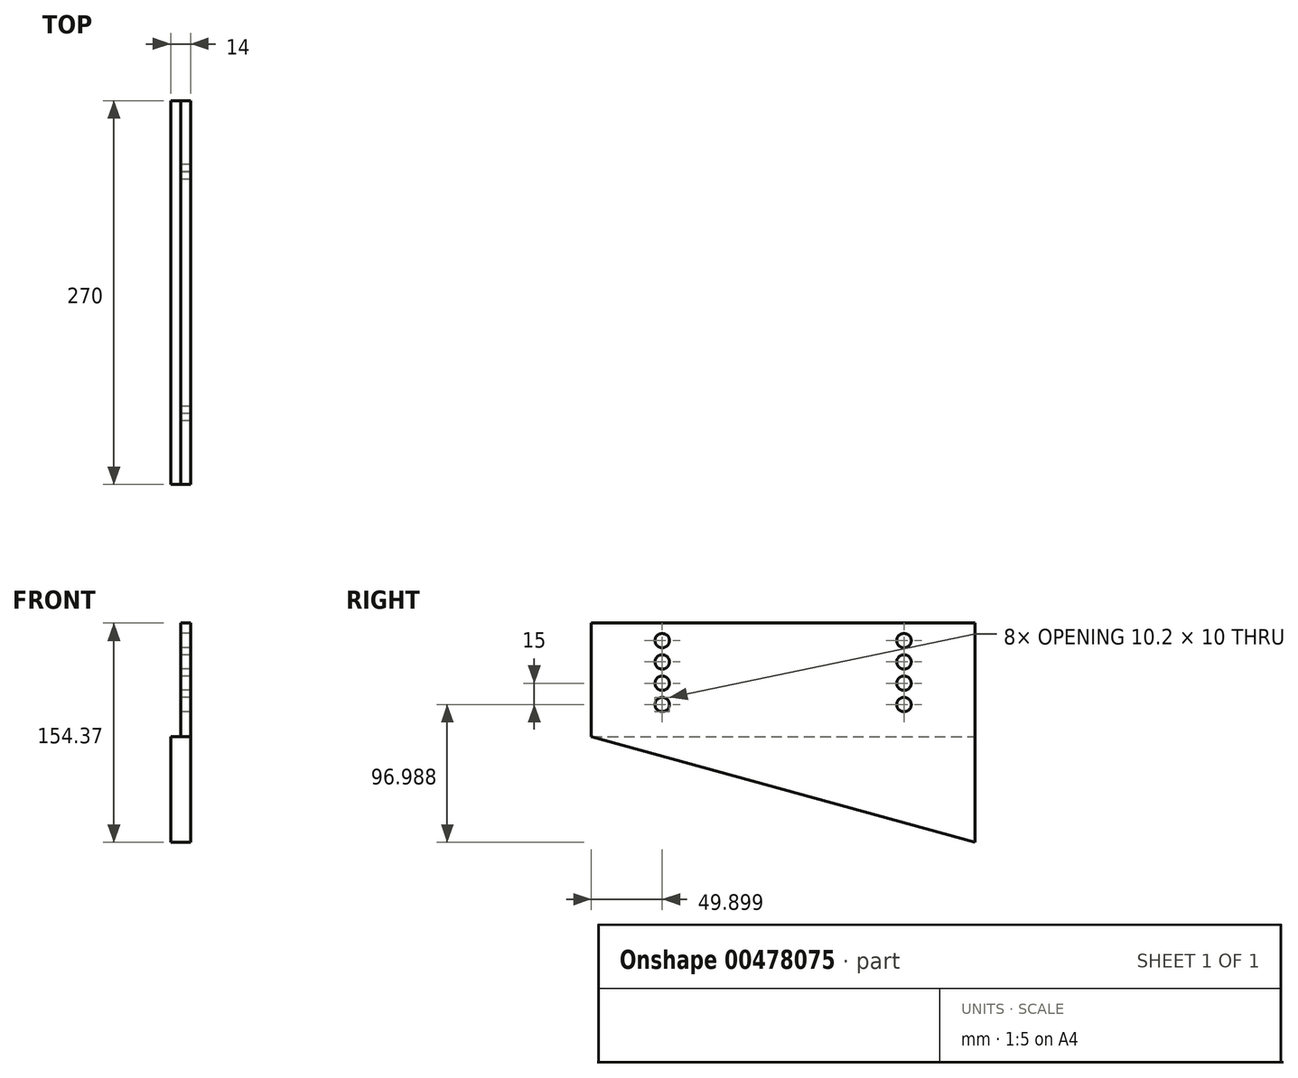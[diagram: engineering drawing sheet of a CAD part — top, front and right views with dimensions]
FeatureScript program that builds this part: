
annotation { "Feature Type Name" : "Feature", "Feature Type Description" : "" }
export const myFeature = defineFeature(function(context is Context, id is Id, definition is map)
    precondition{}
    {
        {
            var Q0;
            Q0=qCreatedBy(makeId("Right.planeOp"),FACE);
            var sketch = newSketch(context, id + "F0", { "sketchPlane" : qUnion([Q0])});
            skLineSegment(sketch, "E0", {"start": v(-152.41, 80) * mm, "end": v(117.59, 80) * mm});
            skLineSegment(sketch, "E1", {"start": v(117.59, -74.37) * mm, "end": v(117.59, 80) * mm});
            skLineSegment(sketch, "E2", {"start": v(-102.41, 80) * mm, "end": v(67.59, 80) * mm});
            skLineSegment(sketch, "E3", {"start": v(117.59, -74.37) * mm, "end": v(-152.41, 0) * mm});
            skLineSegment(sketch, "E4", {"start": v(117.59, 0) * mm, "end": v(-152.41, 0) * mm});
            skLineSegment(sketch, "E5", {"start": v(-152.41, 80) * mm, "end": v(-152.41, 0) * mm});
            skCircle(sketch, "E6", {"center": v(-102.41, 67.62) * mm, "radius": 5 * mm});
            skCircle(sketch, "E7", {"center": v(67.59, 67.62) * mm, "radius": 5 * mm});
            skCircle(sketch, "E8.0.1.0", {"center": v(67.59, 52.62) * mm, "radius": 5 * mm});
            skCircle(sketch, "E8.0.1.1", {"center": v(-102.41, 52.62) * mm, "radius": 5 * mm});
            skCircle(sketch, "E8.0.2.0", {"center": v(67.59, 37.62) * mm, "radius": 5 * mm});
            skCircle(sketch, "E8.0.2.1", {"center": v(-102.41, 37.62) * mm, "radius": 5 * mm});
            skCircle(sketch, "E8.0.3.0", {"center": v(67.59, 22.62) * mm, "radius": 5 * mm});
            skCircle(sketch, "E8.0.3.1", {"center": v(-102.41, 22.62) * mm, "radius": 5 * mm});
            skCircle(sketch, "E8.1.0.0", {"center": v(67.49, 67.62) * mm, "radius": 5 * mm});
            skCircle(sketch, "E8.1.0.1", {"center": v(-102.51, 67.62) * mm, "radius": 5 * mm});
            skCircle(sketch, "E8.1.1.0", {"center": v(67.49, 52.62) * mm, "radius": 5 * mm});
            skCircle(sketch, "E8.1.1.1", {"center": v(-102.51, 52.62) * mm, "radius": 5 * mm});
            skCircle(sketch, "E8.1.2.0", {"center": v(67.49, 37.62) * mm, "radius": 5 * mm});
            skCircle(sketch, "E8.1.2.1", {"center": v(-102.51, 37.62) * mm, "radius": 5 * mm});
            skCircle(sketch, "E8.1.3.0", {"center": v(67.49, 22.62) * mm, "radius": 5 * mm});
            skCircle(sketch, "E8.1.3.1", {"center": v(-102.51, 22.62) * mm, "radius": 5 * mm});
            skCircle(sketch, "E8.2.0.0", {"center": v(67.39, 67.62) * mm, "radius": 5 * mm});
            skCircle(sketch, "E8.2.0.1", {"center": v(-102.61, 67.62) * mm, "radius": 5 * mm});
            skCircle(sketch, "E8.2.1.0", {"center": v(67.39, 52.62) * mm, "radius": 5 * mm});
            skCircle(sketch, "E8.2.1.1", {"center": v(-102.61, 52.62) * mm, "radius": 5 * mm});
            skCircle(sketch, "E8.2.2.0", {"center": v(67.39, 37.62) * mm, "radius": 5 * mm});
            skCircle(sketch, "E8.2.2.1", {"center": v(-102.61, 37.62) * mm, "radius": 5 * mm});
            skCircle(sketch, "E8.2.3.0", {"center": v(67.39, 22.62) * mm, "radius": 5 * mm});
            skCircle(sketch, "E8.2.3.1", {"center": v(-102.61, 22.62) * mm, "radius": 5 * mm});
            skLineSegment(sketch, "E8.direction1", {"start": v(67.59, 67.62) * mm, "end": v(67.49, 67.62) * mm, "construction": true});
            skLineSegment(sketch, "E8.direction2", {"start": v(67.59, 67.62) * mm, "end": v(67.59, 52.62) * mm, "construction": true});
            skSolve(sketch);
        }
        {
            var Q0;
            {var subQ0=sQuery(id+"F0.wireOp",EDGE,"E5");Q0=makeQuery(id+"F0.imprint","IMPRINT",FACE,{"disambiguationData":[TD([[makeQuery(id+"F0.imprint","IMPRINT",EDGE,{"derivedFrom":subQ0}),1.0]])]});}
            var Q1;
            {var subQ5=sQuery(id+"F0.wireOp",EDGE,"kZBZgwTT-XFhY-glHP-XGmq-IiVmHmRIZegb");var subQ6=sQuery(id+"F0.wireOp",EDGE,"E4");var subQ7=makeQuery(id+"F0.imprint","INTERSECT",VERTEX,{"derivedFrom":[subQ6,subQ5]});Q1=makeQuery(id+"F0.imprint","IMPRINT",FACE,{"disambiguationData":[TD([[makeQuery(id+"F0.imprint","IMPRINT",EDGE,{"disambiguationData":[TD([[subQ7,1.0]])],"derivedFrom":subQ6}),-1.0]])]});}
            var Q2;
            {var subQ1=sQuery(id+"F0.wireOp",EDGE,"E2");Q2=makeQuery(id+"F0.imprint","IMPRINT",FACE,{"disambiguationData":[TD([[makeQuery(id+"F0.imprint","IMPRINT",EDGE,{"derivedFrom":subQ1}),-1.0]])]});}
            var Q3;
            {var subQ1=sQuery(id+"F0.wireOp",EDGE,"E0");var subQ5=sQuery(id+"F0.wireOp",EDGE,"E1");var subQ6=makeQuery(id+"F0.imprint","INTERSECT",VERTEX,{"derivedFrom":[subQ1,subQ5]});Q3=makeQuery(id+"F0.imprint","IMPRINT",FACE,{"disambiguationData":[TD([[makeQuery(id+"F0.imprint","IMPRINT",EDGE,{"disambiguationData":[TD([[subQ6,1.0]])],"derivedFrom":subQ5}),1.0]])]});}
            var Q4;
            {var subQ4=sQuery(id+"F0.wireOp",EDGE,"E3");Q4=makeQuery(id+"F0.imprint","IMPRINT",FACE,{"disambiguationData":[TD([[makeQuery(id+"F0.imprint","IMPRINT",EDGE,{"derivedFrom":subQ4}),-1.0]])]});}
            extrude(context, id + "F1", {"entities" : qUnion([Q0, Q1, Q2, Q3, Q4]), "depth" : 7 * mm});
        }
        {
            var Q0;
            Q0=makeQuery(id+"F1.opExtrude","CAP_FACE",FACE,{"disambiguationData":[OSD([sQuery(id+"F0.wireOp",EDGE,"E0"),sQuery(id+"F0.wireOp",EDGE,"E1"),sQuery(id+"F0.wireOp",EDGE,"E2"),sQuery(id+"F0.wireOp",EDGE,"E3"),sQuery(id+"F0.wireOp",EDGE,"E5"),sQuery(id+"F0.wireOp",EDGE,"E6"),sQuery(id+"F0.wireOp",EDGE,"E7")])],"isStart":true});
            var sketch = newSketch(context, id + "F2", { "sketchPlane" : qUnion([Q0])});
            skLineSegment(sketch, "E9", {"start": v(152.41, 0) * mm, "end": v(-117.59, 0) * mm});
            skLineSegment(sketch, "E10", {"start": v(-117.59, 0) * mm, "end": v(-117.59, -74.37) * mm});
            skLineSegment(sketch, "E11", {"start": v(-117.59, -74.37) * mm, "end": v(152.41, 0) * mm});
            skSolve(sketch);
        }
        {
            var Q0;
            Q0=makeQuery(id+"F2.imprint","IMPRINT",FACE,{"disambiguationData":[TD([[makeQuery(id+"F2.imprint","IMPRINT",EDGE,{"derivedFrom":sQuery(id+"F2.wireOp",EDGE,"E9")}),1.0]])]});
            extrude(context, id + "F3", {"entities" : qUnion([Q0]), "operationType" : NewBodyOperationType.ADD, "depth" : 7 * mm});
        }
    });
